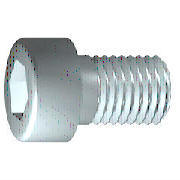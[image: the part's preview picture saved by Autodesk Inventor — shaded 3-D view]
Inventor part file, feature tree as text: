
AUTODESK INVENTOR PART (.ipt)
format: ipt  version: 2017 (Build 210142000, 142)  size: 196,608 bytes
history: native  units: mm (DEFAULTED — no unit token found)
features: sketch x2, extrude x1, plane x1, fillet x1
ambient origin geometry x7: Origin, YZ Plane, XY Plane, X Axis, Y Axis, Z Axis, Center Point
bodies: Solid1 (feature_tree), Body (feature_tree)
feature tree (5):
  extrude  "Slot"  Depth=5.0mm
  plane  "Work Plane1"
  fillet  "Fillet2"  Radius=5.0mm
  sketch  "Sketch1"  dims[d1=5.90924mm d2=0.49086mm d3=5.0mm]
  sketch  "Sketch2"  dims[d4=2.5mm d5=60.0deg d6=5.0mm d7=5.0mm d8=4.618802mm d9=8.5mm d10=90.0deg d11=10.0mm d12=0.0mm d13=5.90924mm d14=0.0mm d15=0.49076mm d16=0.49076mm d17=0.5mm d19=0.0mm d26=8.0mm d27=45.0deg d28=0.0mm d29=0.0mm d30=0.1mm]
